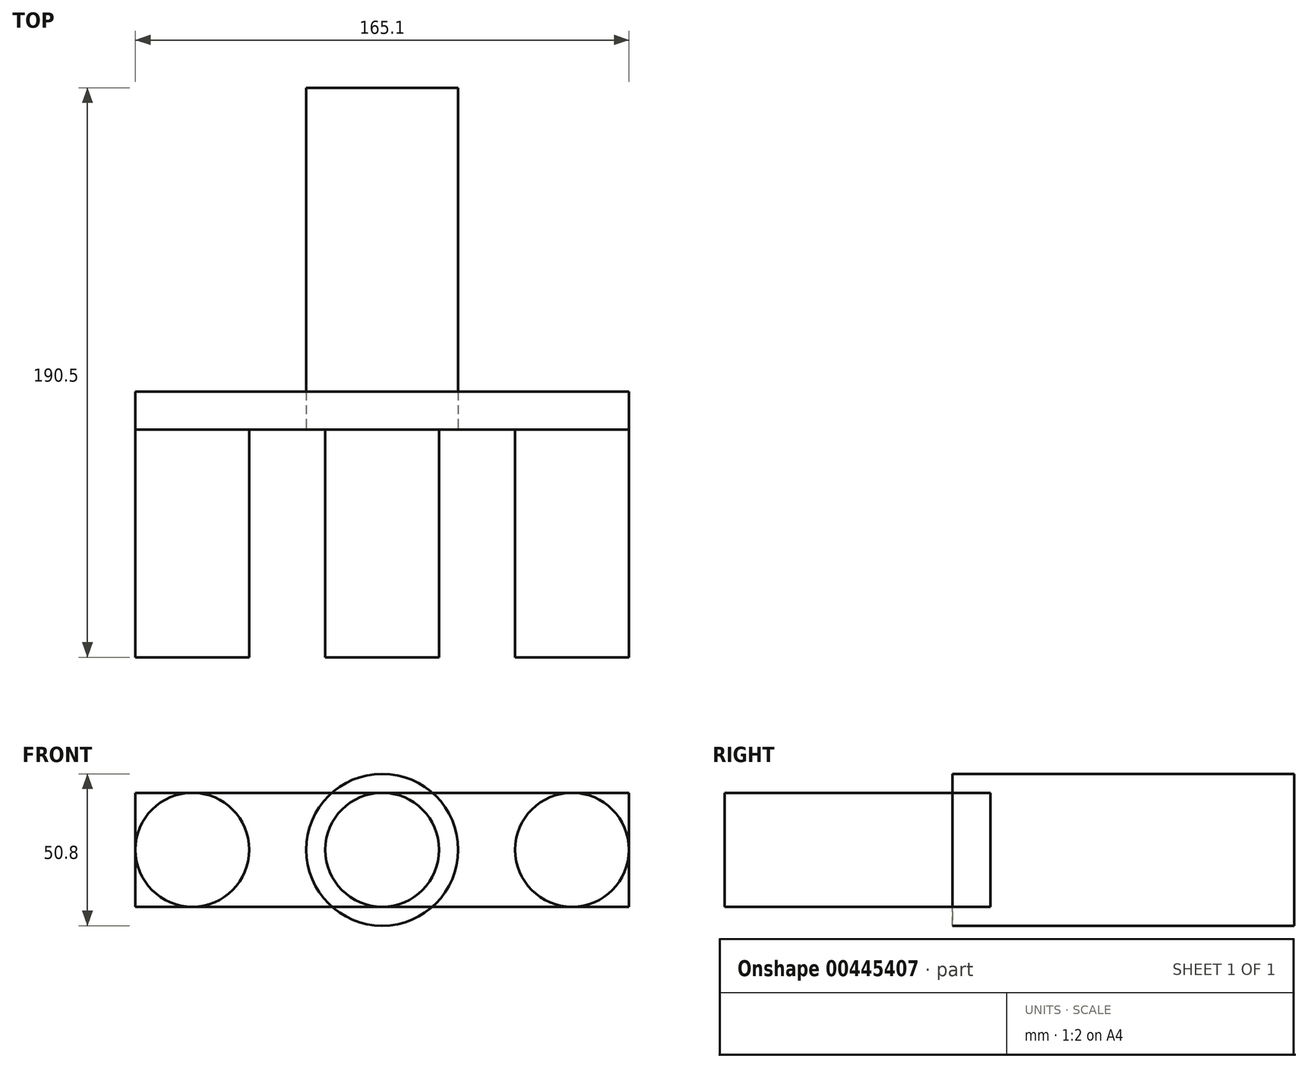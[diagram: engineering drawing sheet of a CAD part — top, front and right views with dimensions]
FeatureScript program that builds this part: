
annotation { "Feature Type Name" : "Feature", "Feature Type Description" : "" }
export const myFeature = defineFeature(function(context is Context, id is Id, definition is map)
    precondition{}
    {
        {
            var Q0;
            Q0=qCreatedBy(makeId("Front.planeOp"),FACE);
            var sketch = newSketch(context, id + "F0", { "sketchPlane" : qUnion([Q0])});
            skCircle(sketch, "E0", {"center": v(0, 0) * mm, "radius": 19.05 * mm});
            skLineSegment(sketch, "E1", {"start": v(0, 0) * mm, "end": v(-63.5, 0) * mm});
            skCircle(sketch, "E2", {"center": v(-63.5, 0) * mm, "radius": 19.05 * mm});
            skLineSegment(sketch, "E3", {"start": v(0, 0) * mm, "end": v(63.5, 0) * mm});
            skCircle(sketch, "E4", {"center": v(63.5, 0) * mm, "radius": 19.05 * mm});
            skLineSegment(sketch, "E5.bottom", {"start": v(-82.55, 19.05) * mm, "end": v(82.55, 19.05) * mm});
            skLineSegment(sketch, "E5.top", {"start": v(-82.55, -19.05) * mm, "end": v(82.55, -19.05) * mm});
            skLineSegment(sketch, "E5.left", {"start": v(-82.55, 19.05) * mm, "end": v(-82.55, -19.05) * mm});
            skLineSegment(sketch, "E5.right", {"start": v(82.55, 19.05) * mm, "end": v(82.55, -19.05) * mm});
            skSolve(sketch);
        }
        {
            var Q0;
            {var subQ0=sQuery(id+"F0.wireOp",EDGE,"E2");var subQ1=makeQuery(id+"F0.imprint","INTERSECT",VERTEX,{"derivedFrom":[sQuery(id+"F0.wireOp",EDGE,"E1"),subQ0]});Q0=makeQuery(id+"F0.imprint","IMPRINT",FACE,{"disambiguationData":[TD([[makeQuery(id+"F0.imprint","IMPRINT",EDGE,{"disambiguationData":[TD([[subQ1,-1.0]])],"derivedFrom":subQ0}),1.0]])]});}
            var Q1;
            {var subQ0=sQuery(id+"F0.wireOp",EDGE,"E0");var subQ1=makeQuery(id+"F0.imprint","INTERSECT",VERTEX,{"derivedFrom":[subQ0,sQuery(id+"F0.wireOp",EDGE,"E5.top")]});Q1=makeQuery(id+"F0.imprint","IMPRINT",FACE,{"disambiguationData":[TD([[makeQuery(id+"F0.imprint","IMPRINT",EDGE,{"disambiguationData":[TD([[subQ1,1.0]])],"derivedFrom":subQ0}),1.0]])]});}
            var Q2;
            {var subQ0=sQuery(id+"F0.wireOp",EDGE,"E4");var subQ1=makeQuery(id+"F0.imprint","INTERSECT",VERTEX,{"derivedFrom":[subQ0,sQuery(id+"F0.wireOp",EDGE,"E5.bottom")]});Q2=makeQuery(id+"F0.imprint","IMPRINT",FACE,{"disambiguationData":[TD([[makeQuery(id+"F0.imprint","IMPRINT",EDGE,{"disambiguationData":[TD([[subQ1,1.0]])],"derivedFrom":subQ0}),1.0]])]});}
            var Q3;
            {var subQ0=sQuery(id+"F0.wireOp",EDGE,"E0");var subQ1=makeQuery(id+"F0.imprint","INTERSECT",VERTEX,{"derivedFrom":[subQ0,sQuery(id+"F0.wireOp",EDGE,"E5.bottom")]});Q3=makeQuery(id+"F0.imprint","IMPRINT",FACE,{"disambiguationData":[TD([[makeQuery(id+"F0.imprint","IMPRINT",EDGE,{"disambiguationData":[TD([[subQ1,1.0]])],"derivedFrom":subQ0}),1.0]])]});}
            extrude(context, id + "F1", {"entities" : qUnion([Q0, Q1, Q2, Q3]), "depth" : 76.2 * mm});
        }
        {
            var Q0;
            {var subQ0=sQuery(id+"F0.wireOp",EDGE,"E0");var subQ1=makeQuery(id+"F0.imprint","INTERSECT",VERTEX,{"derivedFrom":[subQ0,sQuery(id+"F0.wireOp",EDGE,"E5.top")]});Q0=makeQuery(id+"F0.imprint","IMPRINT",FACE,{"disambiguationData":[TD([[makeQuery(id+"F0.imprint","IMPRINT",EDGE,{"disambiguationData":[TD([[subQ1,1.0]])],"derivedFrom":subQ0}),1.0]])]});}
            var Q1;
            {var subQ0=sQuery(id+"F0.wireOp",EDGE,"E0");var subQ1=makeQuery(id+"F0.imprint","INTERSECT",VERTEX,{"derivedFrom":[subQ0,sQuery(id+"F0.wireOp",EDGE,"E5.bottom")]});Q1=makeQuery(id+"F0.imprint","IMPRINT",FACE,{"disambiguationData":[TD([[makeQuery(id+"F0.imprint","IMPRINT",EDGE,{"disambiguationData":[TD([[subQ1,1.0]])],"derivedFrom":subQ0}),1.0]])]});}
            var Q2;
            {var subQ0=sQuery(id+"F0.wireOp",EDGE,"E2");var subQ1=makeQuery(id+"F0.imprint","INTERSECT",VERTEX,{"derivedFrom":[sQuery(id+"F0.wireOp",EDGE,"E1"),subQ0]});Q2=makeQuery(id+"F0.imprint","IMPRINT",FACE,{"disambiguationData":[TD([[makeQuery(id+"F0.imprint","IMPRINT",EDGE,{"disambiguationData":[TD([[subQ1,-1.0]])],"derivedFrom":subQ0}),1.0]])]});}
            var Q3;
            {var subQ0=sQuery(id+"F0.wireOp",EDGE,"E5.bottom");var subQ1=sQuery(id+"F0.wireOp",EDGE,"E0");var subQ2=makeQuery(id+"F0.imprint","INTERSECT",VERTEX,{"derivedFrom":[subQ1,subQ0]});Q3=makeQuery(id+"F0.imprint","IMPRINT",FACE,{"disambiguationData":[TD([[makeQuery(id+"F0.imprint","IMPRINT",EDGE,{"disambiguationData":[TD([[subQ2,-1.0]])],"derivedFrom":subQ1}),-1.0]])]});}
            var Q4;
            {var subQ0=sQuery(id+"F0.wireOp",EDGE,"E5.top");var subQ1=sQuery(id+"F0.wireOp",EDGE,"E0");var subQ2=makeQuery(id+"F0.imprint","INTERSECT",VERTEX,{"derivedFrom":[subQ1,subQ0]});Q4=makeQuery(id+"F0.imprint","IMPRINT",FACE,{"disambiguationData":[TD([[makeQuery(id+"F0.imprint","IMPRINT",EDGE,{"disambiguationData":[TD([[subQ2,1.0]])],"derivedFrom":subQ1}),-1.0]])]});}
            var Q5;
            {var subQ0=sQuery(id+"F0.wireOp",EDGE,"E5.left");var subQ1=sQuery(id+"F0.wireOp",EDGE,"E2");var subQ2=makeQuery(id+"F0.imprint","INTERSECT",VERTEX,{"derivedFrom":[subQ1,subQ0]});Q5=makeQuery(id+"F0.imprint","IMPRINT",FACE,{"disambiguationData":[TD([[makeQuery(id+"F0.imprint","IMPRINT",EDGE,{"disambiguationData":[TD([[subQ2,-1.0]])],"derivedFrom":subQ1}),-1.0]])]});}
            var Q6;
            {var subQ0=sQuery(id+"F0.wireOp",EDGE,"E5.bottom");var subQ1=sQuery(id+"F0.wireOp",EDGE,"E2");var subQ2=makeQuery(id+"F0.imprint","INTERSECT",VERTEX,{"derivedFrom":[subQ1,subQ0]});Q6=makeQuery(id+"F0.imprint","IMPRINT",FACE,{"disambiguationData":[TD([[makeQuery(id+"F0.imprint","IMPRINT",EDGE,{"disambiguationData":[TD([[subQ2,-1.0]])],"derivedFrom":subQ1}),-1.0]])]});}
            var Q7;
            {var subQ0=sQuery(id+"F0.wireOp",EDGE,"E5.bottom");var subQ1=sQuery(id+"F0.wireOp",EDGE,"E0");var subQ2=makeQuery(id+"F0.imprint","INTERSECT",VERTEX,{"derivedFrom":[subQ1,subQ0]});Q7=makeQuery(id+"F0.imprint","IMPRINT",FACE,{"disambiguationData":[TD([[makeQuery(id+"F0.imprint","IMPRINT",EDGE,{"disambiguationData":[TD([[subQ2,1.0]])],"derivedFrom":subQ1}),-1.0]])]});}
            var Q8;
            {var subQ0=sQuery(id+"F0.wireOp",EDGE,"E5.top");var subQ1=sQuery(id+"F0.wireOp",EDGE,"E0");var subQ2=makeQuery(id+"F0.imprint","INTERSECT",VERTEX,{"derivedFrom":[subQ1,subQ0]});Q8=makeQuery(id+"F0.imprint","IMPRINT",FACE,{"disambiguationData":[TD([[makeQuery(id+"F0.imprint","IMPRINT",EDGE,{"disambiguationData":[TD([[subQ2,-1.0]])],"derivedFrom":subQ1}),-1.0]])]});}
            var Q9;
            {var subQ0=sQuery(id+"F0.wireOp",EDGE,"E4");var subQ1=makeQuery(id+"F0.imprint","INTERSECT",VERTEX,{"derivedFrom":[subQ0,sQuery(id+"F0.wireOp",EDGE,"E5.bottom")]});Q9=makeQuery(id+"F0.imprint","IMPRINT",FACE,{"disambiguationData":[TD([[makeQuery(id+"F0.imprint","IMPRINT",EDGE,{"disambiguationData":[TD([[subQ1,1.0]])],"derivedFrom":subQ0}),1.0]])]});}
            var Q10;
            {var subQ0=sQuery(id+"F0.wireOp",EDGE,"E5.right");var subQ1=sQuery(id+"F0.wireOp",EDGE,"E4");var subQ2=makeQuery(id+"F0.imprint","INTERSECT",VERTEX,{"derivedFrom":[subQ1,subQ0]});Q10=makeQuery(id+"F0.imprint","IMPRINT",FACE,{"disambiguationData":[TD([[makeQuery(id+"F0.imprint","IMPRINT",EDGE,{"disambiguationData":[TD([[subQ2,1.0]])],"derivedFrom":subQ1}),-1.0]])]});}
            var Q11;
            {var subQ0=sQuery(id+"F0.wireOp",EDGE,"E5.bottom");var subQ1=sQuery(id+"F0.wireOp",EDGE,"E4");var subQ2=makeQuery(id+"F0.imprint","INTERSECT",VERTEX,{"derivedFrom":[subQ1,subQ0]});Q11=makeQuery(id+"F0.imprint","IMPRINT",FACE,{"disambiguationData":[TD([[makeQuery(id+"F0.imprint","IMPRINT",EDGE,{"disambiguationData":[TD([[subQ2,1.0]])],"derivedFrom":subQ1}),-1.0]])]});}
            extrude(context, id + "F2", {"entities" : qUnion([Q0, Q1, Q2, Q3, Q4, Q5, Q6, Q7, Q8, Q9, Q10, Q11]), "oppositeDirection" : true, "depth" : 12.7 * mm});
        }
        {
            var Q0;
            Q0=qCreatedBy(makeId("Front.planeOp"),FACE);
            var sketch = newSketch(context, id + "F3", { "sketchPlane" : qUnion([Q0])});
            skCircle(sketch, "E6", {"center": v(0, 0) * mm, "radius": 25.4 * mm});
            skSolve(sketch);
        }
        {
            var Q0;
            Q0 = qSketchRegion(id + "F3", true);
            extrude(context, id + "F4", {"entities" : qUnion([Q0]), "oppositeDirection" : true, "depth" : 114.3 * mm});
        }
    });
